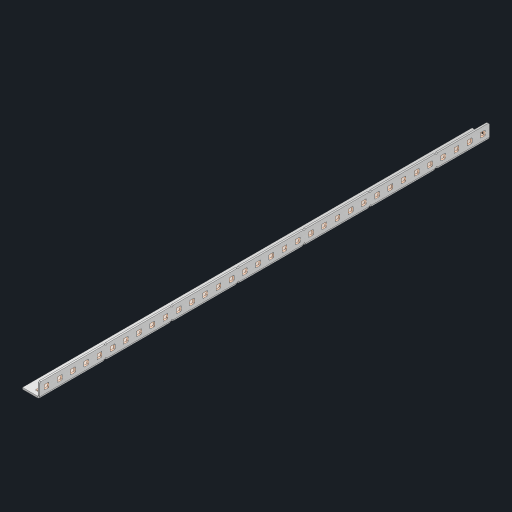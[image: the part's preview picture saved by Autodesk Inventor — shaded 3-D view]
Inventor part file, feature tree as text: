
AUTODESK INVENTOR PART (.ipt)
format: ipt  version: 2023 (Build 270158000, 158)  size: 1,044,480 bytes
history: native  units: in
note: dims shown in document units (in); Inventor stores cm internally (conversion verified against a paired STEP export)
features: other x73, extrude x67, sheet_metal_op x10, sketch x8, mirror x1, pattern_linear x1, chamfer x1
ambient origin geometry x8: Origin, YZ Plane, XZ Plane, XY Plane, X Axis, Y Axis, Z Axis, Center Point
bodies: Solid1 (feature_tree), Body (feature_tree)
feature tree (161):
  other  "Flange Pattern Plane"
  sheet_metal_op  "Flange Pattern"
  sheet_metal_op  "Body Pattern"
  other  "Arc Length"
  mirror  "Notch Mirror"
  pattern_linear  "Notch Pattern"  Spacing1=0.25in  [1 undecoded]
  chamfer  "End Chamfer"
  extrude  "Half Cut"  Depth=0.0625in
  sketch  "Sketch1"  dims[d0=1.5in]
  other  "Plate1"
  sketch  "Sketch2"  dims[d1=17.0in]
  other  "Plate2"
  sheet_metal_op  "Bend1"
  sheet_metal_op  "Corner1"
  sketch  "Sketch3"  dims[d2=0.0625in]
  other  "Flange Pattern Sketch"
  sketch  "Sketch7"  dims[d3=0.0625in]
  other  "Srf1"
  other  "Srf2"
  sketch  "Sketch8"  dims[d4=0.0312in]
  sketch  "Sketch9"  dims[d5=0.125in]
  other  "Srf91"
  sheet_metal_op  "Body Pattern Sketch"
  other  "Srf92"
  sketch  "Sketch13"  dims[d6=0.0625in]
  sketch  "Sketch14"  dims[d7=0.5in d8=90.0deg d9=0.0312in d10=0.25in d11=0.0625in d12=0.0625in d16=0.182in d17=0.02in d18=0.0625in d19=0.0in d20=0.25in d21=0.25in d46=0.172in d47=1.0in d48=0.0in d49=0.182in d50=0.02in d51=0.25in d52=0.25in d53=0.0625in d54=0.0in d55=0.172in d56=1.0in d57=0.0in d60=13.3858in d62=0.5in d63=0.3937in d65=0.5in d85=0.1473in d86=0.1782in d88=0.04in d89=0.0625in d90=0.0in d91=0.04in d92=0.0491in d95=2.5in d96=0.04in d97=0.25in d98=45.0deg d101=0.0in d102=2.497in d131=0.5in d132=13.3858in d134=0.5in d139=0.5in]
  other  "Srf856"
  other  "Srf1310"
  other  "Srf1311"
  other  "Srf1312"
  other  "Srf1376"
  other  "Srf1377"
  other  "Srf1728"
  other  "Srf1755"
  other  "Srf1878"
  other  "Srf1879"
  other  "Srf1880"
  other  "Srf1881"
  other  "Srf1882"
  other  "Srf1883"
  other  "Srf1884"
  other  "Srf1885"
  other  "Srf1886"
  other  "Srf1887"
  other  "Srf1888"
  other  "Srf1889"
  other  "Srf1890"
  other  "Srf1891"
  other  "Srf1892"
  other  "Srf1893"
  other  "Srf1894"
  other  "Srf1895"
  other  "Srf1896"
  other  "Srf1897"
  other  "Srf1898"
  other  "Srf1899"
  other  "Srf1900"
  other  "Srf1901"
  other  "Srf1902"
  other  "Srf1903"
  other  "Srf1904"
  other  "Srf1905"
  other  "Srf1942"
  other  "Srf1943"
  other  "Srf1944"
  other  "Srf1945"
  other  "Srf1946"
  other  "Srf1947"
  other  "Srf1948"
  other  "Srf1949"
  other  "Srf1950"
  other  "Srf1951"
  other  "Srf1952"
  other  "Srf1953"
  other  "Srf1954"
  other  "Srf1955"
  other  "Srf1956"
  other  "Srf1957"
  other  "Srf1958"
  other  "Srf1959"
  other  "Srf1960"
  other  "Srf1961"
  other  "Srf1962"
  other  "Srf1963"
  other  "Srf1964"
  other  "Srf1965"
  other  "Srf1966"
  other  "Srf1967"
  other  "Srf1968"
  other  "Srf1969"
  sheet_metal_op  "Flange Stamp"
  sheet_metal_op  "Flange Circle"
  sheet_metal_op  "Body Stamp"
  sheet_metal_op  "Body Circle"
  sheet_metal_op  "Notch"
  extrude  "ExtrusionSrf2"  Depth=0.0625in
  extrude  "ExtrusionSrf92"  Depth=0.5in
  extrude  "ExtrusionSrf856"  Depth=0.02in
  extrude  "ExtrusionSrf1310"  Depth=0.0625in
  extrude  "ExtrusionSrf1311"  TaperAngle=0.0deg  [1 undecoded]
  extrude  "ExtrusionSrf1312"  Depth=0.5in
  extrude  "ExtrusionSrf1376"  Depth=0.5in
  extrude  "ExtrusionSrf1377"  Depth=0.5in
  extrude  "ExtrusionSrf1728"  Depth=0.5in TaperAngle=0.0deg
  extrude  "ExtrusionSrf1755"  Depth=0.5in
  extrude  "ExtrusionSrf1878"  Depth=0.02in
  extrude  "ExtrusionSrf1879"  Depth=0.5in
  extrude  "ExtrusionSrf1880"  Depth=0.5in
  extrude  "ExtrusionSrf1881"  Depth=0.0625in
  extrude  "ExtrusionSrf1882"  TaperAngle=0.0deg  [1 undecoded]
  extrude  "ExtrusionSrf1883"  Depth=0.5in
  extrude  "ExtrusionSrf1884"  Depth=0.5in TaperAngle=0.0deg
  extrude  "ExtrusionSrf1885"  Depth=0.5in
  extrude  "ExtrusionSrf1886"  Depth=0.5in
  extrude  "ExtrusionSrf1887"  Depth=0.5in
  extrude  "ExtrusionSrf1888"  Depth=0.5in
  extrude  "ExtrusionSrf1889"  Depth=0.5in
  extrude  "ExtrusionSrf1890"  Depth=0.0625in
  extrude  "ExtrusionSrf1891"  TaperAngle=0.0deg  [1 undecoded]
  extrude  "ExtrusionSrf1892"  Depth=0.5in
  extrude  "ExtrusionSrf1893"  Depth=0.5in
  extrude  "ExtrusionSrf1894"  Depth=0.5in
  extrude  "ExtrusionSrf1895"  Depth=0.5in TaperAngle=45.0deg
  extrude  "ExtrusionSrf1896"  TaperAngle=0.0deg  [1 undecoded]
  extrude  "ExtrusionSrf1897"  Depth=0.5in
  extrude  "ExtrusionSrf1898"  Depth=0.5in
  extrude  "ExtrusionSrf1899"  Depth=0.5in
  extrude  "ExtrusionSrf1900"  Depth=0.5in
  extrude  "ExtrusionSrf1901"  Depth=0.5in
  extrude  "ExtrusionSrf1902"  [1 undecoded]
  extrude  "ExtrusionSrf1903"  [1 undecoded]
  extrude  "ExtrusionSrf1904"  [1 undecoded]
  extrude  "ExtrusionSrf1905"  [1 undecoded]
  extrude  "ExtrusionSrf1942"  [1 undecoded]
  extrude  "ExtrusionSrf1943"  [1 undecoded]
  extrude  "ExtrusionSrf1944"  [1 undecoded]
  extrude  "ExtrusionSrf1945"  [1 undecoded]
  extrude  "ExtrusionSrf1946"  [1 undecoded]
  extrude  "ExtrusionSrf1947"  [1 undecoded]
  extrude  "ExtrusionSrf1948"  [1 undecoded]
  extrude  "ExtrusionSrf1949"  [1 undecoded]
  extrude  "ExtrusionSrf1950"  [1 undecoded]
  extrude  "ExtrusionSrf1951"  [1 undecoded]
  extrude  "ExtrusionSrf1952"  [1 undecoded]
  extrude  "ExtrusionSrf1953"  [1 undecoded]
  extrude  "ExtrusionSrf1954"  [1 undecoded]
  extrude  "ExtrusionSrf1955"  [1 undecoded]
  extrude  "ExtrusionSrf1956"  [1 undecoded]
  extrude  "ExtrusionSrf1957"  [1 undecoded]
  extrude  "ExtrusionSrf1958"  [1 undecoded]
  extrude  "ExtrusionSrf1959"  [1 undecoded]
  extrude  "ExtrusionSrf1960"  [1 undecoded]
  extrude  "ExtrusionSrf1961"  [1 undecoded]
  extrude  "ExtrusionSrf1962"  [1 undecoded]
  extrude  "ExtrusionSrf1963"  [1 undecoded]
  extrude  "ExtrusionSrf1964"  [1 undecoded]
  extrude  "ExtrusionSrf1965"  [1 undecoded]
  extrude  "ExtrusionSrf1966"  [1 undecoded]
  extrude  "ExtrusionSrf1967"  [1 undecoded]
  extrude  "ExtrusionSrf1968"  [1 undecoded]
  extrude  "ExtrusionSrf1969"  [1 undecoded]
note: 37 required parameter values undecoded (feature->parameter linkage not recoverable at this tier; creation-order binding heuristic only, values carry confidence <= 0.55)
